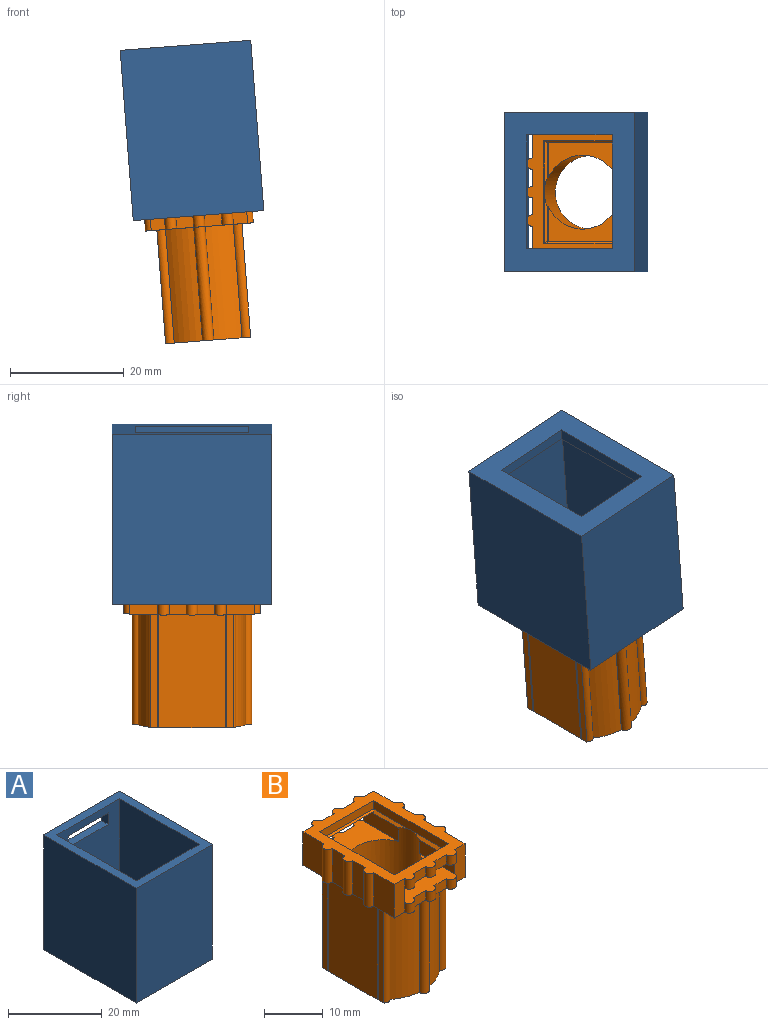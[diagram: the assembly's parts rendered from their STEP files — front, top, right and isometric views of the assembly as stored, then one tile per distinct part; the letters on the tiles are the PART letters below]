
ASSEMBLY  parts=2 mates=1
PART A: 24 faces, bbox 23x28x30 mm
  f0: plane 30x23mm, normal (0,-1,0), area 690mm2, adj f1,f3,f5,f14
  f1: plane 30x28mm, normal (1,0,0), area 840mm2, adj f0,f2,f5,f14
  f2: plane 30x23mm, normal (0,1,0), area 654mm2, adj f1,f3,f5,f14,f15,f16,f17,f18
  f3: plane 30x28mm, normal (-1,0,0), area 840mm2, adj f0,f2,f5,f14
  f4: plane 24x19mm, normal (0,0,1), area 156mm2, adj f6,f7,f8,f9,f10,f11,f12,f13
  f5: plane 28x23mm, normal (0,0,-1), area 344mm2, adj f0,f1,f2,f3,f6,f7,f8,f9
  f6: plane 15x2mm, normal (0,1,0), area 30mm2, adj f4,f5,f7,f9
  f7: plane 20x2mm, normal (-1,0,0), area 40mm2, adj f4,f5,f6,f8
  f8: plane 15x2mm, normal (0,-1,0), area 30mm2, adj f4,f5,f7,f9
  f9: plane 20x2mm, normal (1,0,0), area 40mm2, adj f4,f5,f6,f8
  f10: plane 28x19mm, normal (0,-1,0), area 496mm2, adj f4,f11,f13,f14,f15,f16,f17,f18
  f11: plane 28x24mm, normal (-1,0,0), area 672mm2, adj f4,f10,f12,f14
  f12: plane 28x19mm, normal (0,1,0), area 510mm2, adj f4,f11,f13,f14,f19,f20,f21,f22
  f13: plane 28x24mm, normal (1,0,0), area 672mm2, adj f4,f10,f12,f14
  f14: plane 28x23mm, normal (0,0,1), area 188mm2, adj f0,f1,f2,f3,f10,f11,f12,f13
  f15: plane 3x2mm, normal (1,0,0), area 6mm2, adj f2,f10,f16,f18
  f16: plane 12x2mm, normal (0,0,-1), area 24mm2, adj f2,f10,f15,f17
  f17: plane 3x2mm, normal (-1,0,0), area 6mm2, adj f2,f10,f16,f18
  f18: plane 12x2mm, normal (0,0,1), area 24mm2, adj f2,f10,f15,f17
  f19: plane 11x2mm, normal (0,0,-1), area 22mm2, adj f12,f20,f22,f23
  f20: plane 2x2mm, normal (-1,0,0), area 4mm2, adj f12,f19,f21,f23
  f21: plane 11x2mm, normal (0,0,1), area 22mm2, adj f12,f20,f22,f23
  f22: plane 2x2mm, normal (1,0,0), area 4mm2, adj f12,f19,f21,f23
  f23: plane 11x2mm, normal (0,1,0), area 22mm2, adj f19,f20,f21,f22
PART B: 84 faces, bbox 19x24x27 mm
  f0: cylinder r=1mm len=2mm, axis (0,0,-1), area 6.3mm2, adj f9,f15,f47,f58
  f1: cylinder r=1mm len=2mm, axis (0,0,-1), area 6.3mm2, adj f2,f13,f23,f58
  f2: plane 3x2mm, normal (0,1,0), area 6mm2, adj f1,f3,f13,f58
  f3: cylinder r=1mm len=2mm, axis (0,0,-1), area 6.3mm2, adj f2,f4,f13,f58
  f4: plane 3x2mm, normal (0,1,0), area 6mm2, adj f3,f5,f13,f58
  f5: cylinder r=1mm len=2mm, axis (0,0,-1), area 6.3mm2, adj f4,f13,f29,f58
  f6: cylinder r=1mm len=2mm, axis (0,0,-1), area 6.3mm2, adj f7,f37,f47,f58
  f7: plane 3x2mm, normal (0,-1,0), area 6mm2, adj f6,f8,f47,f58
  f8: cylinder r=1mm len=2mm, axis (0,0,-1), area 6.3mm2, adj f7,f9,f47,f58
  f9: plane 3x2mm, normal (0,-1,0), area 6mm2, adj f0,f8,f47,f58
  f10: cylinder r=6.5mm len=25.3mm, axis (0,0,-1), area 930.6mm2, adj f11,f12,f13,f47,f74,f76,f77,f78
  f11: plane 9x0.5mm, normal (0.71,0,0.71), area 5mm2, adj f10,f43,f73,f82
  f12: plane 9x0.5mm, normal (0.71,0,0.71), area 5mm2, adj f10,f43,f75,f79
  f13: plane 12x9.5mm, normal (0,0,1), area 72mm2, adj f1,f2,f3,f4,f5,f10,f78,f79
  f14: cylinder r=1mm len=2mm, axis (0,0,-1), area 6.3mm2, adj f15,f41,f42,f81
  f15: plane 7x2.5mm, normal (0,-1,0), area 17.5mm2, adj f0,f14,f16,f42,f58,f83
  f16: plane 7x5mm, normal (1,0,0), area 35mm2, adj f15,f17,f42,f58
  f17: cylinder r=1mm len=7mm, axis (0,0,-1), area 22mm2, adj f16,f18,f42,f58
  f18: plane 7x3mm, normal (1,0,0), area 21mm2, adj f17,f19,f42,f58
  f19: cylinder r=1mm len=7mm, axis (0,0,-1), area 22mm2, adj f18,f20,f42,f58
  f20: plane 7x3mm, normal (1,0,0), area 21mm2, adj f19,f21,f42,f58
  f21: cylinder r=1mm len=7mm, axis (0,0,-1), area 22mm2, adj f20,f22,f42,f58
  f22: plane 7x5mm, normal (1,0,0), area 35mm2, adj f21,f23,f42,f58
  f23: plane 7x2.5mm, normal (0,1,0), area 17.5mm2, adj f1,f22,f24,f42,f58,f78
  f24: cylinder r=1mm len=2mm, axis (0,0,-1), area 6.3mm2, adj f23,f25,f42,f80
  f25: plane 3x2mm, normal (0,1,0), area 6mm2, adj f24,f26,f42,f80
  f26: cylinder r=1mm len=2mm, axis (0,0,-1), area 6.3mm2, adj f25,f27,f42,f80
  f27: plane 3x2mm, normal (0,1,0), area 6mm2, adj f26,f28,f42,f80
  f28: cylinder r=1mm len=2mm, axis (0,0,-1), area 6.3mm2, adj f27,f29,f42,f80
  f29: plane 7x2.5mm, normal (0,1,0), area 17.5mm2, adj f5,f28,f30,f42,f58,f79
  f30: plane 7x5mm, normal (-1,0,0), area 35mm2, adj f29,f31,f42,f58
  f31: cylinder r=1mm len=7mm, axis (0,0,-1), area 22mm2, adj f30,f32,f42,f58
  f32: plane 7x3mm, normal (-1,0,0), area 21mm2, adj f31,f33,f42,f58
  f33: cylinder r=1mm len=7mm, axis (0,0,-1), area 22mm2, adj f32,f34,f42,f58
  f34: plane 7x3mm, normal (-1,0,0), area 21mm2, adj f33,f35,f42,f58
  f35: cylinder r=1mm len=7mm, axis (0,0,-1), area 22mm2, adj f34,f36,f42,f58
  f36: plane 7x5mm, normal (-1,0,0), area 35mm2, adj f35,f37,f42,f58
  f37: plane 7x2.5mm, normal (0,-1,0), area 17.5mm2, adj f6,f36,f38,f42,f58,f82
  f38: cylinder r=1mm len=2mm, axis (0,0,-1), area 6.3mm2, adj f37,f39,f42,f81
  f39: plane 3x2mm, normal (0,-1,0), area 6mm2, adj f38,f40,f42,f81
  f40: cylinder r=1mm len=2mm, axis (0,0,-1), area 6.3mm2, adj f39,f41,f42,f81
  f41: plane 3x2mm, normal (0,-1,0), area 6mm2, adj f14,f40,f42,f81
  f42: plane 24x19mm, normal (0,0,1), area 158.8mm2, adj f14,f15,f16,f17,f18,f19,f20,f21
  f43: plane 18x1.7mm, normal (1,0,0), area 30.6mm2, adj f11,f12,f42,f44,f46
  f44: plane 13x1.7mm, normal (0,-1,0), area 22.1mm2, adj f42,f43,f45,f75
  f45: plane 18x1.7mm, normal (-1,0,0), area 30.6mm2, adj f42,f44,f46,f74,f76
  f46: plane 13x1.7mm, normal (0,1,0), area 22.1mm2, adj f42,f43,f45,f73
  f47: plane 12x9.5mm, normal (0,0,1), area 72mm2, adj f0,f6,f7,f8,f9,f10,f82,f83
  f48: cylinder r=1mm len=20mm, axis (0,0,1), area 34.7mm2, adj f58,f69,f71,f77
  f49: cylinder r=1mm len=20mm, axis (0,0,1), area 3.3mm2, adj f50,f58,f69,f77
  f50: cylinder r=9.5mm len=20mm, axis (0,0,1), area 3.7mm2, adj f49,f58,f68,f77
  f51: cylinder r=9.5mm len=20mm, axis (0,0,1), area 3.7mm2, adj f52,f58,f68,f77
  f52: cylinder r=1mm len=20mm, axis (0,0,1), area 3.3mm2, adj f51,f58,f67,f77
  f53: cylinder r=1mm len=20mm, axis (0,0,1), area 34.7mm2, adj f58,f61,f67,f77
  f54: cylinder r=1mm len=20mm, axis (0,0,1), area 34.7mm2, adj f58,f63,f70,f77
  f55: cylinder r=1mm len=20mm, axis (0,0,1), area 3.3mm2, adj f56,f58,f70,f77
  f56: cylinder r=9.5mm len=20mm, axis (0,0,1), area 3.7mm2, adj f55,f58,f64,f77
  f57: cylinder r=9.5mm len=20mm, axis (0,0,1), area 3.7mm2, adj f58,f59,f64,f77
  f58: plane 24x19mm, normal (0,0,-1), area 132.2mm2, adj f0,f1,f2,f3,f4,f5,f6,f7
  f59: cylinder r=1mm len=20mm, axis (0,0,1), area 3.3mm2, adj f57,f58,f65,f77
  f60: cylinder r=1mm len=20mm, axis (0,0,1), area 34.7mm2, adj f58,f62,f65,f77
  f61: cylinder r=9.5mm len=20mm, axis (0,0,1), area 109.2mm2, adj f53,f58,f66,f77
  f62: cylinder r=9.5mm len=20mm, axis (0,0,1), area 109.2mm2, adj f58,f60,f66,f77
  f63: cylinder r=9.5mm len=20mm, axis (0,0,1), area 109.2mm2, adj f54,f58,f72,f77
  f64: plane 20x11.66mm, normal (1,0,0), area 233.2mm2, adj f56,f57,f58,f77
  f65: plane 20x1.25mm, normal (1,0,0), area 24.9mm2, adj f58,f59,f60,f77
  f66: cylinder r=1mm len=20mm, axis (0,0,1), area 64.9mm2, adj f58,f61,f62,f77
  f67: plane 20x1.25mm, normal (-1,0,0), area 24.9mm2, adj f52,f53,f58,f77
  f68: plane 20x11.66mm, normal (-1,0,0), area 233.2mm2, adj f50,f51,f58,f77
  f69: plane 20x1.25mm, normal (-1,0,0), area 24.9mm2, adj f48,f49,f58,f77
  f70: plane 20x1.25mm, normal (1,0,0), area 24.9mm2, adj f54,f55,f58,f77
  f71: cylinder r=9.5mm len=20mm, axis (0,0,1), area 109.2mm2, adj f48,f58,f72,f77
  f72: cylinder r=1mm len=20mm, axis (0,0,1), area 64.9mm2, adj f58,f63,f71,f77
  f73: plane 13x0.5mm, normal (0,0.71,0.71), area 5.4mm2, adj f11,f46,f74,f81,f82,f83
  f74: plane 9x0.5mm, normal (-0.71,0,0.71), area 5mm2, adj f10,f45,f73,f83
  f75: plane 13x0.5mm, normal (0,-0.71,0.71), area 5.4mm2, adj f12,f44,f76,f78,f79,f80
  f76: plane 9x0.5mm, normal (-0.71,0,0.71), area 5mm2, adj f10,f45,f75,f78
  f77: plane 21x15mm, normal (0,0,-1), area 127.9mm2, adj f10,f48,f49,f50,f51,f52,f53,f54
  f78: plane 8.5x3mm, normal (-1,0,0), area 24.3mm2, adj f10,f13,f23,f75,f76,f80
  f79: plane 8.5x3mm, normal (1,0,0), area 24.3mm2, adj f10,f12,f13,f29,f75,f80
  f80: plane 12x3.3mm, normal (0,0,-1), area 32.3mm2, adj f24,f25,f26,f27,f28,f75,f78,f79
  f81: plane 12x3.3mm, normal (0,0,-1), area 32.3mm2, adj f14,f38,f39,f40,f41,f73,f82,f83
  f82: plane 8.5x3mm, normal (1,0,0), area 24.3mm2, adj f10,f11,f37,f47,f73,f81
  f83: plane 8.5x3mm, normal (-1,0,0), area 24.3mm2, adj f10,f15,f47,f73,f74,f81
PLACE A rot(axis=(0,1,0),175.6deg) t=(3.52,0,19.51)mm
PLACE B rot(axis=(0,-1,0),4.4deg) t=(5.81,0,-10.4)mm
MATE fastened B.f10 <-> A.f18  axis (-0.08,0,1) through (5.43,0,-5.41)mm
